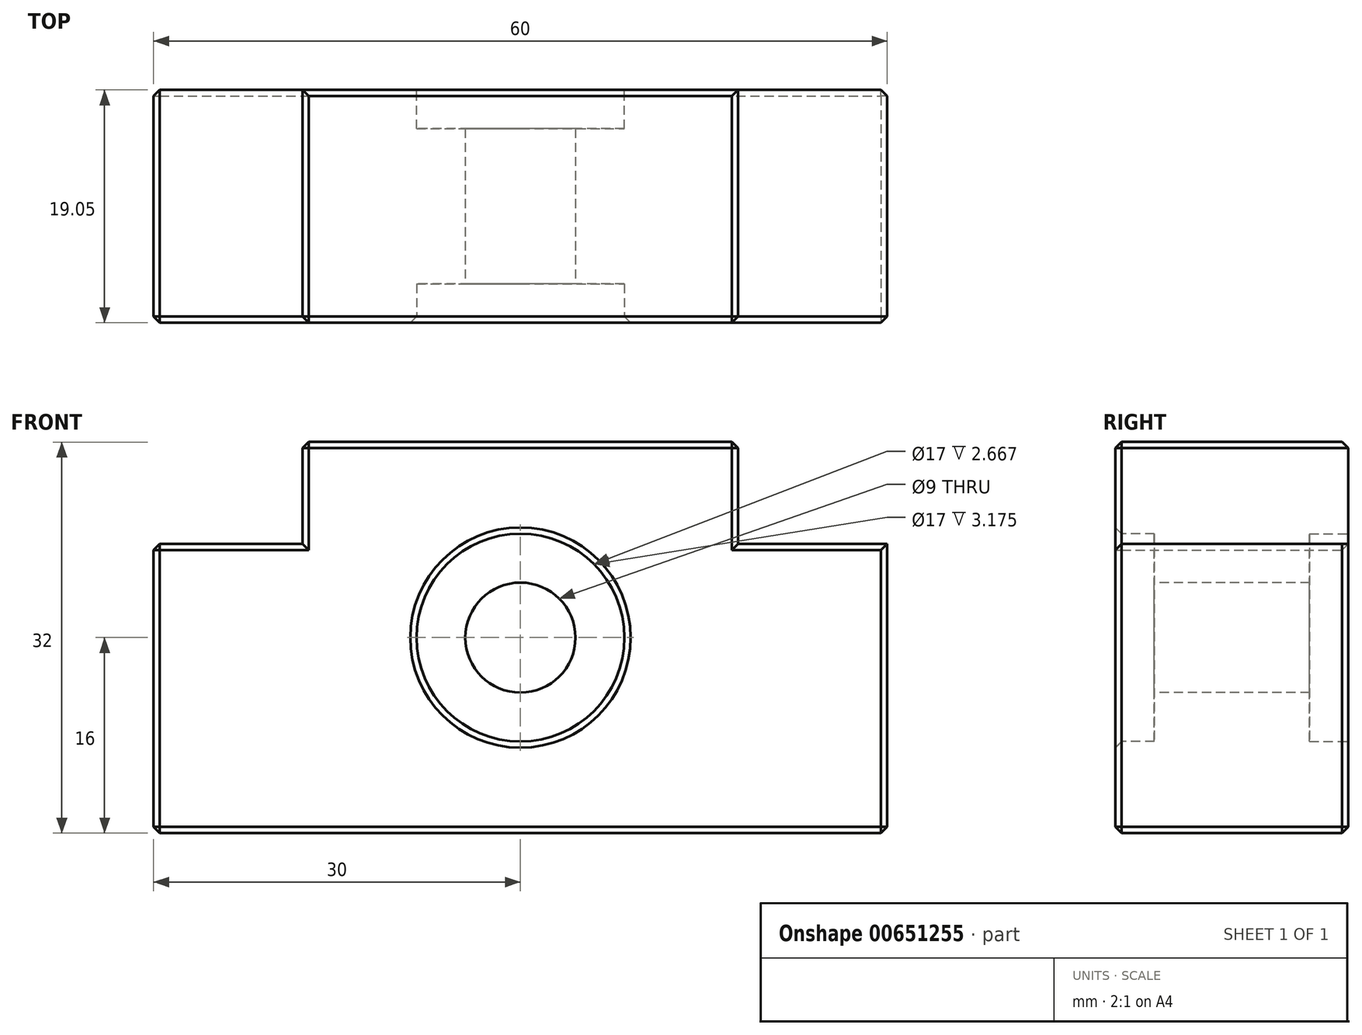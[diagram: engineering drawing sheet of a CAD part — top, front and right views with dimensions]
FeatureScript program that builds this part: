
annotation { "Feature Type Name" : "Feature", "Feature Type Description" : "" }
export const myFeature = defineFeature(function(context is Context, id is Id, definition is map)
    precondition{}
    {
        {
            var Q0;
            Q0=qCreatedBy(makeId("Front.planeOp"),FACE);
            var sketch = newSketch(context, id + "F0", { "sketchPlane" : qUnion([Q0])});
            skLineSegment(sketch, "E0", {"start": v(0, -16) * mm, "end": v(-30, -16) * mm});
            skLineSegment(sketch, "E1.MirrorCS", {"start": v(0, -16) * mm, "end": v(30, -16) * mm});
            skLineSegment(sketch, "E2", {"start": v(-30, -16) * mm, "end": v(-30, 7.67) * mm});
            skLineSegment(sketch, "E3.MirrorCS", {"start": v(30, -16) * mm, "end": v(30, 7.67) * mm});
            skLineSegment(sketch, "E4", {"start": v(0, 16) * mm, "end": v(-17.81, 16) * mm});
            skLineSegment(sketch, "E5", {"start": v(0, 16) * mm, "end": v(17.81, 16) * mm});
            skLineSegment(sketch, "E6", {"start": v(-17.81, 16) * mm, "end": v(-17.81, 7.67) * mm});
            skLineSegment(sketch, "E7", {"start": v(-17.81, 7.67) * mm, "end": v(-30, 7.67) * mm});
            skLineSegment(sketch, "E8.MirrorCS", {"start": v(17.81, 7.67) * mm, "end": v(30, 7.67) * mm});
            skLineSegment(sketch, "E9.MirrorCS", {"start": v(17.81, 16) * mm, "end": v(17.81, 7.67) * mm});
            skSolve(sketch);
        }
        {
            var Q0;
            Q0=makeQuery(id+"F0.imprint","IMPRINT",FACE,{"disambiguationData":[TD([[makeQuery(id+"F0.imprint","IMPRINT",EDGE,{"derivedFrom":sQuery(id+"F0.wireOp",EDGE,"E0")}),-1.0]])]});
            extrude(context, id + "F1", {"entities" : qUnion([Q0]), "depth" : 19.05 * mm, "offsetDistance" : 25.4 * mm});
        }
        {
            var Q0;
            Q0=makeQuery(id+"F1.opExtrude","CAP_FACE",FACE,{"disambiguationData":[OSD([sQuery(id+"F0.wireOp",EDGE,"E0"),sQuery(id+"F0.wireOp",EDGE,"E1.MirrorCS"),sQuery(id+"F0.wireOp",EDGE,"E2"),sQuery(id+"F0.wireOp",EDGE,"E3.MirrorCS"),sQuery(id+"F0.wireOp",EDGE,"E4"),sQuery(id+"F0.wireOp",EDGE,"E5"),sQuery(id+"F0.wireOp",EDGE,"E6"),sQuery(id+"F0.wireOp",EDGE,"E7"),sQuery(id+"F0.wireOp",EDGE,"E8.MirrorCS"),sQuery(id+"F0.wireOp",EDGE,"E9.MirrorCS")])],"isStart":false});
            var sketch = newSketch(context, id + "F2", { "sketchPlane" : qUnion([Q0])});
            skCircle(sketch, "E10", {"center": v(0, 0) * mm, "radius": 8.5 * mm});
            skSolve(sketch);
        }
        {
            var Q0;
            Q0=makeQuery(id+"F2.imprint","IMPRINT",FACE,{"disambiguationData":[TD([[makeQuery(id+"F2.imprint","IMPRINT",EDGE,{"derivedFrom":sQuery(id+"F2.wireOp",EDGE,"E10")}),1.0]])]});
            extrude(context, id + "F3", {"entities" : qUnion([Q0]), "operationType" : NewBodyOperationType.REMOVE, "oppositeDirection" : true, "depth" : 3.17 * mm, "offsetDistance" : 25.4 * mm});
        }
        {
            var Q0;
            Q0=makeQuery(id+"F3.boolean.opBoolean","COPY",FACE,{"derivedFrom":makeQuery(id+"F3.opExtrude","CAP_FACE",FACE,{"disambiguationData":[OSD([sQuery(id+"F2.wireOp",EDGE,"E10")])],"isStart":false})});
            var sketch = newSketch(context, id + "F4", { "sketchPlane" : qUnion([Q0])});
            skCircle(sketch, "E11", {"center": v(0, 0) * mm, "radius": 4.5 * mm});
            skSolve(sketch);
        }
        {
            var Q0;
            Q0=makeQuery(id+"F4.imprint","IMPRINT",FACE,{"disambiguationData":[TD([[makeQuery(id+"F4.imprint","IMPRINT",EDGE,{"derivedFrom":sQuery(id+"F4.wireOp",EDGE,"E11")}),1.0]])]});
            var Q1;
            Q1=makeQuery(id+"F1.opExtrude","CAP_FACE",FACE,{"disambiguationData":[OSD([sQuery(id+"F0.wireOp",EDGE,"E0"),sQuery(id+"F0.wireOp",EDGE,"E1.MirrorCS"),sQuery(id+"F0.wireOp",EDGE,"E2"),sQuery(id+"F0.wireOp",EDGE,"E3.MirrorCS"),sQuery(id+"F0.wireOp",EDGE,"E4"),sQuery(id+"F0.wireOp",EDGE,"E5"),sQuery(id+"F0.wireOp",EDGE,"E6"),sQuery(id+"F0.wireOp",EDGE,"E7"),sQuery(id+"F0.wireOp",EDGE,"E8.MirrorCS"),sQuery(id+"F0.wireOp",EDGE,"E9.MirrorCS")])],"isStart":true});
            extrude(context, id + "F5", {"entities" : qUnion([Q0]), "operationType" : NewBodyOperationType.REMOVE, "endBound" : BoundingType.UP_TO_SURFACE, "oppositeDirection" : true, "depth" : 25.4 * mm, "endBoundEntityFace" : qUnion([Q1]), "offsetDistance" : 25.4 * mm});
        }
        {
            var Q0;
            Q0=qCreatedBy(makeId("Front.planeOp"),FACE);
            var sketch = newSketch(context, id + "F6", { "sketchPlane" : qUnion([Q0])});
            skCircle(sketch, "E12", {"center": v(0, 0) * mm, "radius": 8.5 * mm});
            skSolve(sketch);
        }
        {
            var Q0;
            Q0=makeQuery(id+"F6.imprint","IMPRINT",FACE,{"disambiguationData":[TD([[makeQuery(id+"F6.imprint","IMPRINT",EDGE,{"derivedFrom":sQuery(id+"F6.wireOp",EDGE,"E12")}),1.0]])]});
            extrude(context, id + "F7", {"entities" : qUnion([Q0]), "operationType" : NewBodyOperationType.REMOVE, "oppositeDirection" : true, "depth" : -3.17 * mm, "offsetDistance" : 25.4 * mm});
        }
        {
            var Q0;
            Q0=makeQuery(id+"F1.opExtrude","SWEPT_EDGE",EDGE,{"disambiguationData":[OSD([sQuery(id+"F0.wireOp",EDGE,"E2"),sQuery(id+"F0.wireOp",EDGE,"E7")])]});
            var Q1;
            Q1=makeQuery(id+"F1.opExtrude","SWEPT_EDGE",EDGE,{"disambiguationData":[OSD([sQuery(id+"F0.wireOp",EDGE,"E4"),sQuery(id+"F0.wireOp",EDGE,"E6")])]});
            var Q2;
            Q2=makeQuery(id+"F1.opExtrude","CAP_EDGE",EDGE,{"disambiguationData":[OSD([sQuery(id+"F0.wireOp",EDGE,"E2")])],"isStart":false});
            var Q3;
            Q3=makeQuery(id+"F1.opExtrude","CAP_EDGE",EDGE,{"disambiguationData":[OSD([sQuery(id+"F0.wireOp",EDGE,"E4")])],"isStart":false});
            var Q4;
            Q4=makeQuery(id+"F1.opExtrude","CAP_EDGE",EDGE,{"disambiguationData":[OSD([sQuery(id+"F0.wireOp",EDGE,"E5")])],"isStart":false});
            var Q5;
            Q5=makeQuery(id+"F1.opExtrude","CAP_EDGE",EDGE,{"disambiguationData":[OSD([sQuery(id+"F0.wireOp",EDGE,"E8.MirrorCS")])],"isStart":false});
            var Q6;
            Q6=makeQuery(id+"F1.opExtrude","CAP_EDGE",EDGE,{"disambiguationData":[OSD([sQuery(id+"F0.wireOp",EDGE,"E3.MirrorCS")])],"isStart":false});
            var Q7;
            Q7=makeQuery(id+"F1.opExtrude","CAP_EDGE",EDGE,{"disambiguationData":[OSD([sQuery(id+"F0.wireOp",EDGE,"E0"),sQuery(id+"F0.wireOp",EDGE,"E1.MirrorCS")])],"isStart":false});
            var Q8;
            Q8=makeQuery(id+"F1.opExtrude","CAP_EDGE",EDGE,{"disambiguationData":[OSD([sQuery(id+"F0.wireOp",EDGE,"E4")])],"isStart":true});
            var Q9;
            Q9=makeQuery(id+"F1.opExtrude","CAP_EDGE",EDGE,{"disambiguationData":[OSD([sQuery(id+"F0.wireOp",EDGE,"E5")])],"isStart":true});
            var Q10;
            Q10=makeQuery(id+"F1.opExtrude","SWEPT_EDGE",EDGE,{"disambiguationData":[OSD([sQuery(id+"F0.wireOp",EDGE,"E5"),sQuery(id+"F0.wireOp",EDGE,"E9.MirrorCS")])]});
            var Q11;
            Q11=makeQuery(id+"F1.opExtrude","CAP_EDGE",EDGE,{"disambiguationData":[OSD([sQuery(id+"F0.wireOp",EDGE,"E2")])],"isStart":true});
            var Q12;
            Q12=makeQuery(id+"F1.opExtrude","CAP_EDGE",EDGE,{"disambiguationData":[OSD([sQuery(id+"F0.wireOp",EDGE,"E3.MirrorCS")])],"isStart":true});
            var Q13;
            Q13=makeQuery(id+"F1.opExtrude","CAP_EDGE",EDGE,{"disambiguationData":[OSD([sQuery(id+"F0.wireOp",EDGE,"E0"),sQuery(id+"F0.wireOp",EDGE,"E1.MirrorCS")])],"isStart":true});
            var Q14;
            Q14=makeQuery(id+"F1.opExtrude","SWEPT_EDGE",EDGE,{"disambiguationData":[OSD([sQuery(id+"F0.wireOp",EDGE,"E1.MirrorCS"),sQuery(id+"F0.wireOp",EDGE,"E3.MirrorCS")])]});
            var Q15;
            Q15=makeQuery(id+"F1.opExtrude","SWEPT_FACE",FACE,{"disambiguationData":[OSD([sQuery(id+"F0.wireOp",EDGE,"E2")])]});
            var Q16;
            Q16=makeQuery(id+"F7.boolean.opBoolean","COPY",EDGE,{"derivedFrom":makeQuery(id+"F7.opExtrude","CAP_EDGE",EDGE,{"disambiguationData":[OSD([sQuery(id+"F6.wireOp",EDGE,"E12")])],"isStart":true})});
            var Q17;
            Q17=makeQuery(id+"F1.opExtrude","CAP_FACE",FACE,{"disambiguationData":[OSD([sQuery(id+"F0.wireOp",EDGE,"E0"),sQuery(id+"F0.wireOp",EDGE,"E1.MirrorCS"),sQuery(id+"F0.wireOp",EDGE,"E2"),sQuery(id+"F0.wireOp",EDGE,"E3.MirrorCS"),sQuery(id+"F0.wireOp",EDGE,"E4"),sQuery(id+"F0.wireOp",EDGE,"E5"),sQuery(id+"F0.wireOp",EDGE,"E6"),sQuery(id+"F0.wireOp",EDGE,"E7"),sQuery(id+"F0.wireOp",EDGE,"E8.MirrorCS"),sQuery(id+"F0.wireOp",EDGE,"E9.MirrorCS")])],"isStart":false});
            chamfer(context, id + "F8", {"entities" : qUnion([Q0, Q1, Q2, Q3, Q4, Q5, Q6, Q7, Q8, Q9, Q10, Q11, Q12, Q13, Q14, Q15, Q16, Q17]), "width" : 0.5 * mm, "tangentPropagation" : true});
        }
    });
